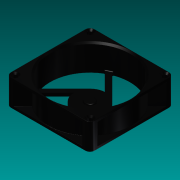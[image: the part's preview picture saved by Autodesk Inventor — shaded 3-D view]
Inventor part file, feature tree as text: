
AUTODESK INVENTOR PART (.ipt)
format: ipt  version: 2015 (Build 190159000, 159)  size: 637,440 bytes
history: native  units: mm
features: fillet x10, sketch x7, extrude x6, chamfer x2, other x2, projected_geometry x1
ambient origin geometry x8: Origin, YZ Plane, XZ Plane, XY Plane, X Axis, Y Axis, Z Axis, Center Point
bodies: Solid1 (feature_tree)
feature tree (28):
  extrude  "Extrusion1"  Depth=78.0mm
  extrude  "Extrusion2"  Depth=80.0mm
  extrude  "Extrusion3"  Depth=40.0mm TaperAngle=360.0deg
  chamfer  "Chamfer1"  Distance=25.0mm
  fillet  "Fillet1"  Radius=76.0mm
  fillet  "Fillet2"  Radius=22.0mm
  fillet  "Fillet3"  Radius=71.5mm
  extrude  "Extrusion4"  Depth=1.0mm
  chamfer  "Chamfer2"  Distance=4.5mm
  extrude  "Extrusion5"  Depth=1.0mm
  fillet  "Fillet4"  Radius=4.5mm
  fillet  "Fillet5"  Radius=25.0mm
  fillet  "Fillet6"  Radius=1.5mm
  fillet  "Fillet7"  Radius=1.0mm
  fillet  "Fillet8"  Radius=1.0mm
  fillet  "Fillet9"  Radius=1.0mm
  extrude  "Extrusion6"  Depth=1.0mm
  fillet  "Fillet10"  Radius=78.5mm
  other  "Decal1"
  sketch  "Sketch1"  dims[d0=30.0mm d1=78.0mm]
  sketch  "Sketch2"  dims[d2=80.0mm d3=80.0mm]
  sketch  "Sketch3"  dims[d4=5.0mm d5=40.0mm d7=360.0deg]
  sketch  "Sketch5"  dims[d9=38.0mm]
  projected_geometry  "Projected Loop1"
  sketch  "Sketch6"  dims[d10=15.0mm]
  sketch  "Sketch7"  dims[d11=4.5mm d12=25.0mm d13=0.0mm d14=76.0mm d15=22.0mm d16=0.0mm d17=71.5mm]
  sketch  "Sketch8"  dims[d18=71.5mm d19=4.5mm d20=4.5mm d21=4.5mm d22=4.5mm d23=25.0mm d24=0.0mm d25=1.5mm d26=2.0mm d27=45.0deg d28=1.0mm d29=1.0mm d30=1.0mm d31=79.0mm d45=78.5mm d46=5.0mm d48=5.0mm d49=5.0mm d50=5.0mm d51=90.0deg d52=47.984586mm d53=65.857864mm d54=40.0mm d55=8.936639mm d56=8.936639mm d57=40.0mm d59=360.0deg d61=20.0mm d62=0.0mm d63=1.5mm d64=2.0mm d65=45.0deg d66=28.0mm d67=1.0mm d68=0.0mm d69=0.3mm d70=0.3mm d71=0.2mm d72=0.2mm d73=0.2mm d74=0.2mm d75=10.0mm d76=1.0mm d77=0.0mm d78=1.0mm]
  other  "Image1"
